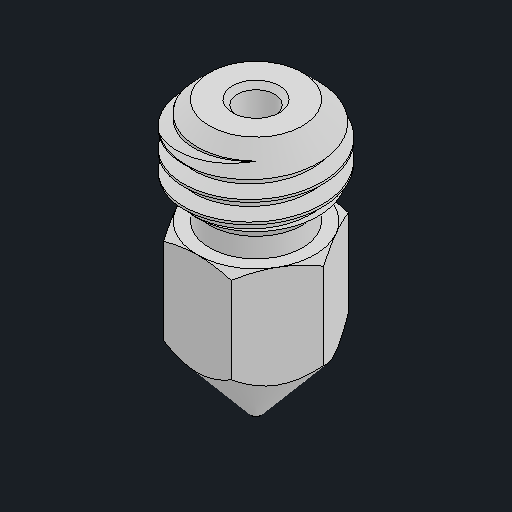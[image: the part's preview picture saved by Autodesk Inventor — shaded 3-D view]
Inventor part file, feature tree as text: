
AUTODESK INVENTOR PART (.ipt)
format: ipt  version: 2024.2 (Build 282272000, 272)  size: 220,160 bytes
history: native  units: mm
features: other x1, chamfer x1
ambient origin geometry x8: Origin, YZ Plane, XZ Plane, XY Plane, X Axis, Y Axis, Z Axis, Center Point
bodies: Body1 (feature_tree)
feature tree (2):
  other  "솔리드1"
  chamfer  "Chamfer1"  [1 undecoded]
note: 1 required parameter value undecoded (feature->parameter linkage not recoverable at this tier; creation-order binding heuristic only, values carry confidence <= 0.55)
